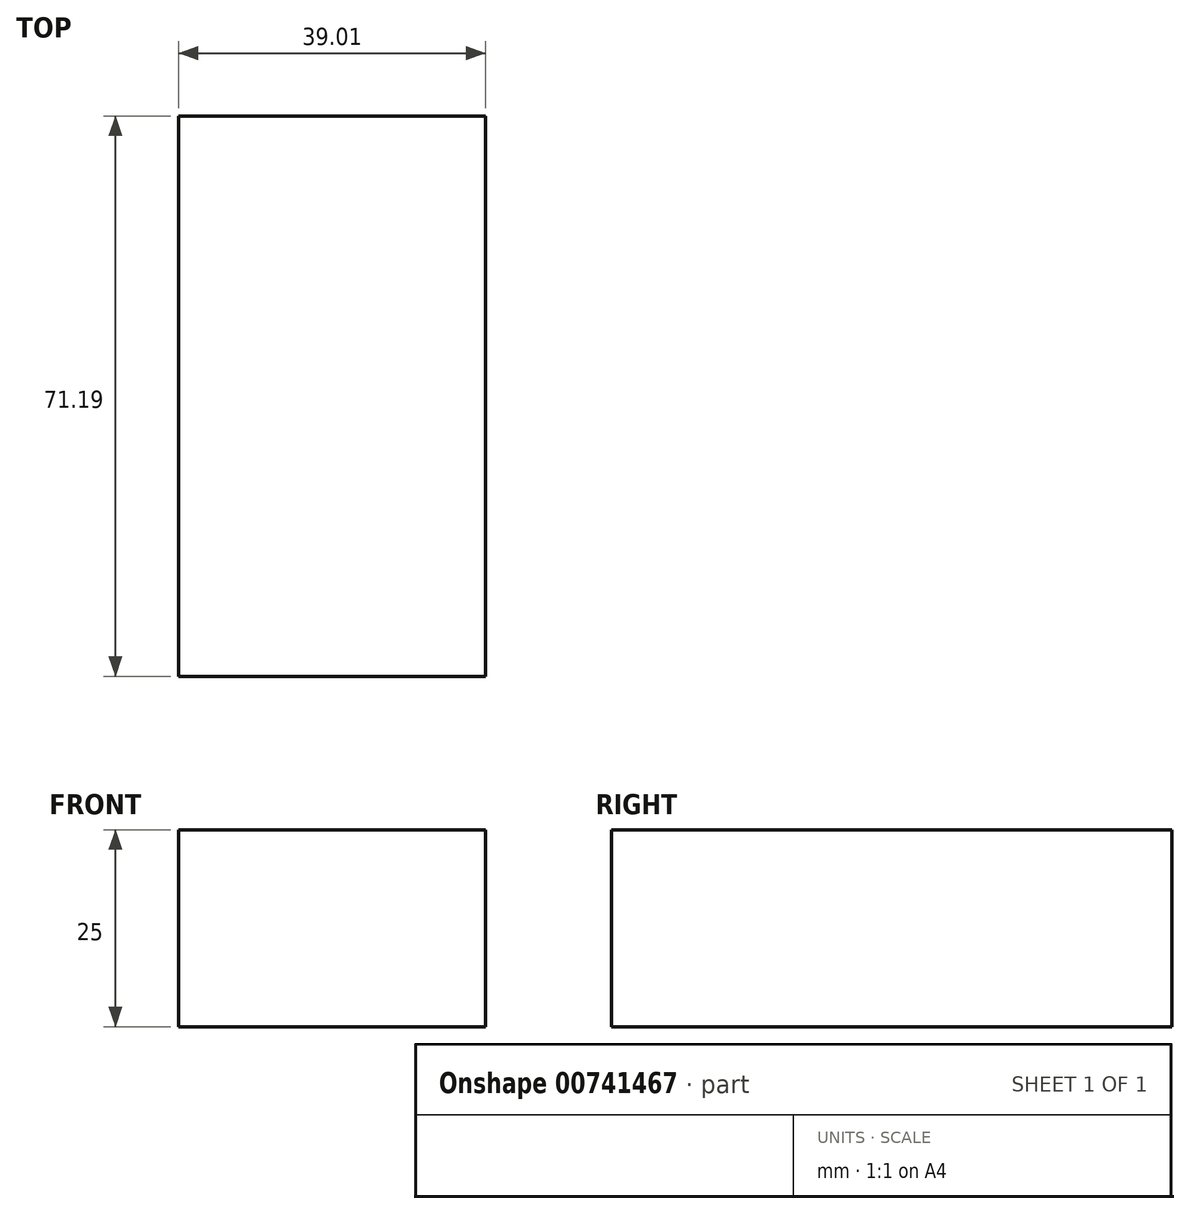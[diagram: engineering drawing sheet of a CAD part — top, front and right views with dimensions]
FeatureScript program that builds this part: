
annotation { "Feature Type Name" : "Feature", "Feature Type Description" : "" }
export const myFeature = defineFeature(function(context is Context, id is Id, definition is map)
    precondition{}
    {
        {
            var Q0;
            Q0=qCreatedBy(makeId("Top.planeOp"),FACE);
            cPlane(context, id + "F0", {"entities" : qUnion([Q0]), "cplaneType" : CPlaneType.OFFSET, "offset" : 125 * mm, "width" : 150 * mm, "height" : 150 * mm});
        }
        {
            var Q0;
            Q0=qCreatedBy(id+"F0.planeOp",FACE);
            var sketch = newSketch(context, id + "F1", { "sketchPlane" : qUnion([Q0])});
            skLineSegment(sketch, "E0.bottom", {"start": v(0, 0) * mm, "end": v(39, 0) * mm});
            skLineSegment(sketch, "E0.top", {"start": v(0, 71.19) * mm, "end": v(39, 71.19) * mm});
            skLineSegment(sketch, "E0.left", {"start": v(0, 0) * mm, "end": v(0, 71.19) * mm});
            skLineSegment(sketch, "E0.right", {"start": v(39, 0) * mm, "end": v(39, 71.19) * mm});
            skLineSegment(sketch, "E1", {"start": v(-68.65, 0) * mm, "end": v(62.47, 0) * mm, "construction": true});
            skPoint(sketch, "E2", {"position": v(0, 0) * mm});
            skSolve(sketch);
        }
        {
            var Q0;
            Q0 = qSketchRegion(id + "F1", true);
            extrude(context, id + "F2", {"entities" : qUnion([Q0]), "depth" : 25 * mm, "offsetDistance" : 25 * mm});
        }
    });
